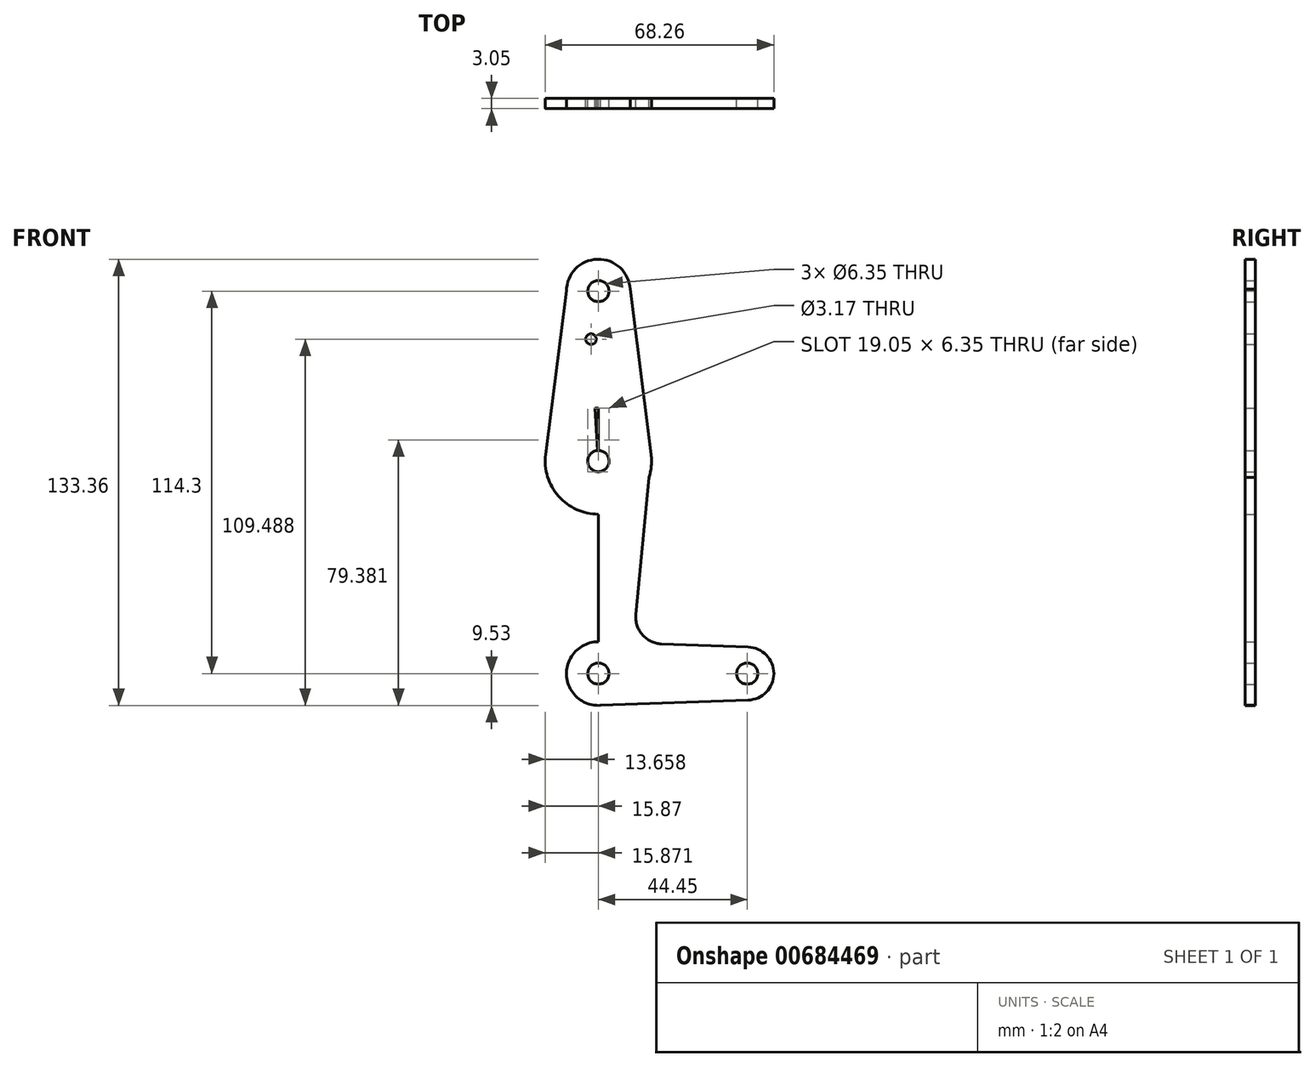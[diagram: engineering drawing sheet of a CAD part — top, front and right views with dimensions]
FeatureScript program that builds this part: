
annotation { "Feature Type Name" : "Feature", "Feature Type Description" : "" }
export const myFeature = defineFeature(function(context is Context, id is Id, definition is map)
    precondition{}
    {
        {
            var Q0;
            Q0=qCreatedBy(makeId("Front.planeOp"),FACE);
            var sketch = newSketch(context, id + "F0", { "sketchPlane" : qUnion([Q0])});
            skCircle(sketch, "E0", {"center": v(0, 63.5) * mm, "radius": 15.88 * mm});
            skLineSegment(sketch, "E1", {"start": v(0, 63.5) * mm, "end": v(0, 0) * mm});
            skCircle(sketch, "E2", {"center": v(0, 0) * mm, "radius": 9.53 * mm});
            skCircle(sketch, "E3", {"center": v(44.45, 0) * mm, "radius": 7.94 * mm});
            skLineSegment(sketch, "E4", {"start": v(44.45, 0) * mm, "end": v(0, 0) * mm});
            skCircle(sketch, "E5", {"center": v(0, 114.3) * mm, "radius": 9.53 * mm});
            skLineSegment(sketch, "E6", {"start": v(0, 114.3) * mm, "end": v(0, 63.5) * mm});
            skLineSegment(sketch, "E7", {"start": v(-9.52, 114.34) * mm, "end": v(-15.75, 65.5) * mm});
            skLineSegment(sketch, "E8", {"start": v(9.5, 114.88) * mm, "end": v(15.75, 65.5) * mm});
            skLineSegment(sketch, "E9", {"start": v(15.75, 65.5) * mm, "end": v(11.22, 17.55) * mm});
            skLineSegment(sketch, "E10", {"start": v(-15.75, 65.5) * mm, "end": v(-9.57, 0) * mm});
            skLineSegment(sketch, "E11", {"start": v(18.86, 8.85) * mm, "end": v(44.73, 7.93) * mm});
            skLineSegment(sketch, "E12", {"start": v(0, -9.53) * mm, "end": v(44.73, -7.93) * mm});
            skCircle(sketch, "E13", {"center": v(0, 114.3) * mm, "radius": 3.18 * mm});
            skCircle(sketch, "E14", {"center": v(0, 63.5) * mm, "radius": 3.18 * mm});
            skCircle(sketch, "E15", {"center": v(0, 0) * mm, "radius": 3.18 * mm});
            skCircle(sketch, "E16", {"center": v(44.45, 0) * mm, "radius": 3.18 * mm});
            skPoint(sketch, "E17.newPointA", {"position": v(9.57, 0) * mm});
            skArc(sketch, "E17.filletArc", {"start": v(11.22, 17.55) * mm, "mid": v(13.16, 11.55) * mm, "end": v(18.86, 8.85) * mm});
            skCircle(sketch, "E18", {"center": v(-2.21, 99.96) * mm, "radius": 1.59 * mm});
            skLineSegment(sketch, "E19", {"start": v(0, 63.5) * mm, "end": v(-2.21, 99.96) * mm});
            skSolve(sketch);
        }
        {
            var Q0;
            Q0 = qSketchRegion(id + "F0", true);
            extrude(context, id + "F1", {"entities" : qUnion([Q0]), "depth" : 3.05 * mm, "offsetDistance" : 25.4 * mm});
        }
    });
